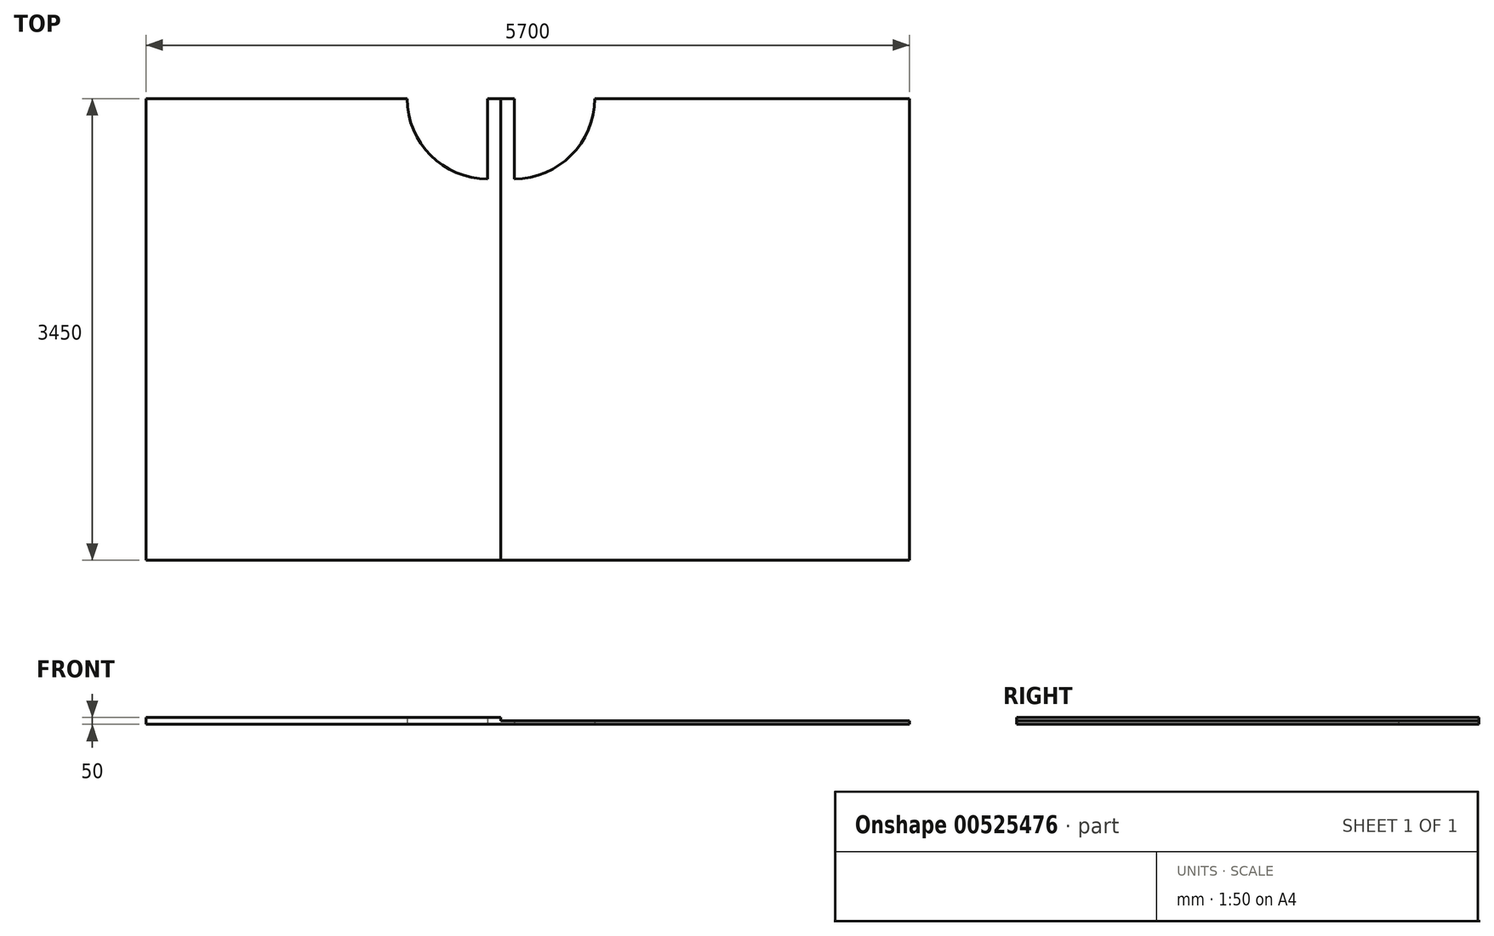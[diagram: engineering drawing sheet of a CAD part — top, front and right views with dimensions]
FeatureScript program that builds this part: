
annotation { "Feature Type Name" : "Feature", "Feature Type Description" : "" }
export const myFeature = defineFeature(function(context is Context, id is Id, definition is map)
    precondition{}
    {
        {
            var Q0;
            Q0=qCreatedBy(makeId("Top.planeOp"),FACE);
            var sketch = newSketch(context, id + "F0", { "sketchPlane" : qUnion([Q0])});
            skLineSegment(sketch, "E0", {"start": v(0, 3450) * mm, "end": v(-5700, 3450) * mm});
            skLineSegment(sketch, "E1", {"start": v(-5700, 3450) * mm, "end": v(-5700, 0) * mm});
            skLineSegment(sketch, "E2", {"start": v(0, 3450) * mm, "end": v(0, 0) * mm});
            skLineSegment(sketch, "E3", {"start": v(-5700, 0) * mm, "end": v(0, 0) * mm});
            skLineSegment(sketch, "E4", {"start": v(-3050, 3450) * mm, "end": v(-3050, 0) * mm});
            skLineSegment(sketch, "E5", {"start": v(-3150, 3450) * mm, "end": v(-3150, 2850) * mm});
            skLineSegment(sketch, "E6", {"start": v(-2950, 3450) * mm, "end": v(-2950, 2850) * mm});
            skArc(sketch, "E7", {"start": v(-3150, 2850) * mm, "mid": v(-3574.26, 3025.74) * mm, "end": v(-3750, 3450) * mm});
            skArc(sketch, "E8", {"start": v(-2950, 2850) * mm, "mid": v(-2525.74, 3025.74) * mm, "end": v(-2350, 3450) * mm});
            skSolve(sketch);
        }
        {
            var Q0;
            {var subQ1=sQuery(id+"F0.wireOp",EDGE,"E2");Q0=makeQuery(id+"F0.imprint","IMPRINT",FACE,{"disambiguationData":[TD([[makeQuery(id+"F0.imprint","IMPRINT",EDGE,{"derivedFrom":subQ1}),-1.0]])]});}
            extrude(context, id + "F1", {"entities" : qUnion([Q0]), "depth" : 25 * mm, "offsetDistance" : 25 * mm});
        }
        {
            var Q0;
            {var subQ0=sQuery(id+"F0.wireOp",EDGE,"E1");Q0=makeQuery(id+"F0.imprint","IMPRINT",FACE,{"disambiguationData":[TD([[makeQuery(id+"F0.imprint","IMPRINT",EDGE,{"derivedFrom":subQ0}),1.0]])]});}
            extrude(context, id + "F2", {"entities" : qUnion([Q0]), "operationType" : NewBodyOperationType.ADD, "depth" : 50 * mm, "offsetDistance" : 25 * mm});
        }
    });
